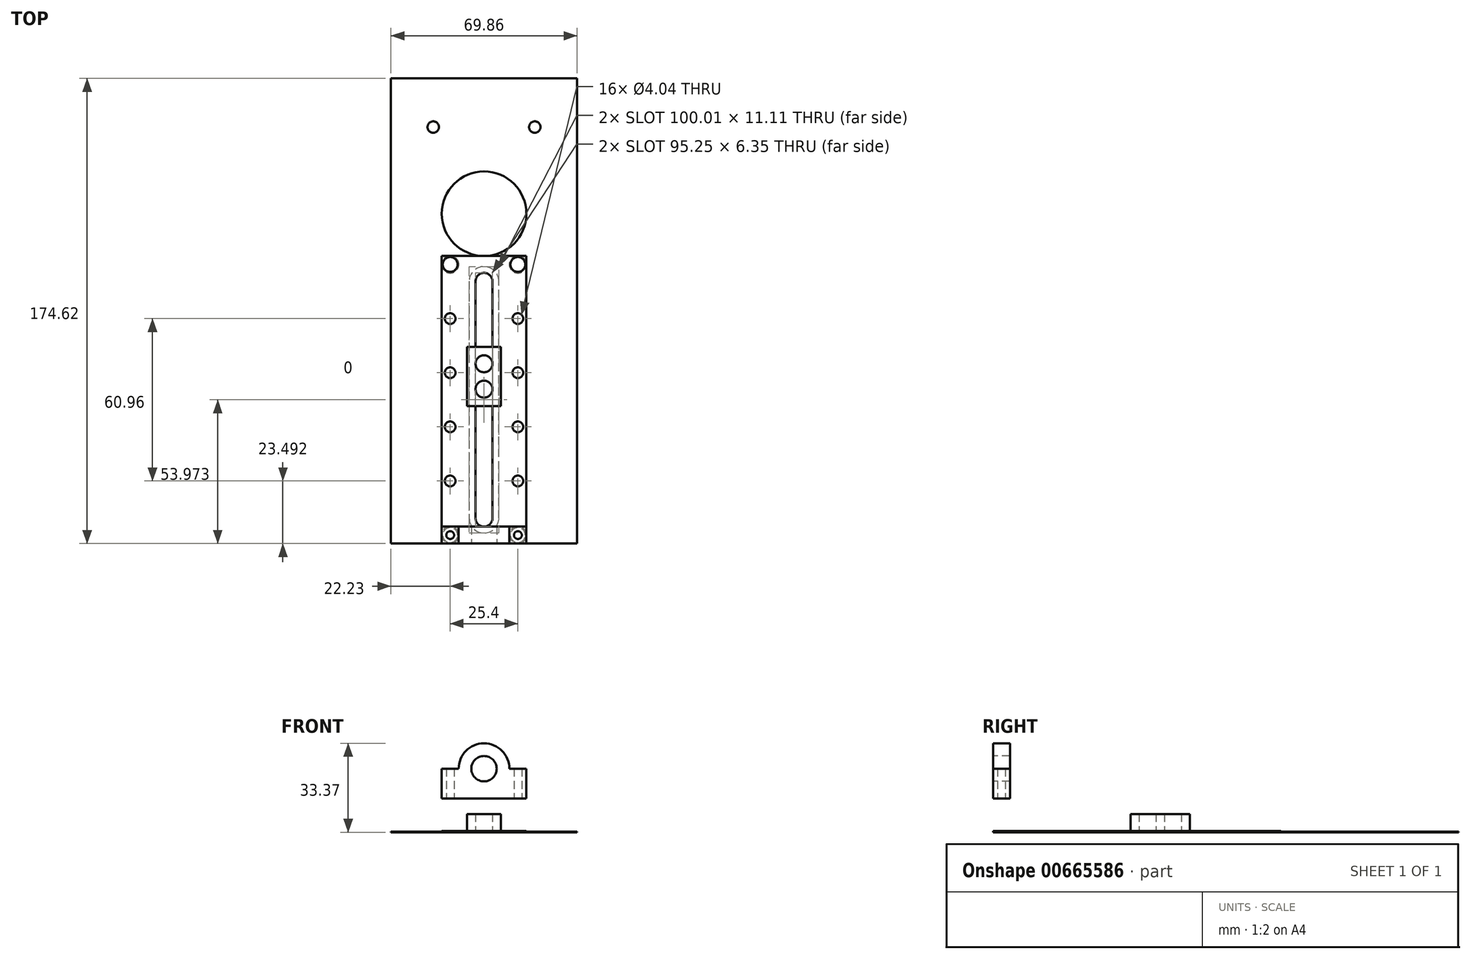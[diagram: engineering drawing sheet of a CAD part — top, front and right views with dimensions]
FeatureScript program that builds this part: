
annotation { "Feature Type Name" : "Feature", "Feature Type Description" : "" }
export const myFeature = defineFeature(function(context is Context, id is Id, definition is map)
    precondition{}
    {
        {
            assignVariable(context, id + "F0", {"name" : "baseThickness", "anyValue" : 0.25});
        }
        {
            assignVariable(context, id + "F1", {"name" : "topThickness", "anyValue" : 0.25});
        }
        {
            var Q0;
            Q0=qCreatedBy(makeId("Top.planeOp"),FACE);
            var sketch = newSketch(context, id + "F2", { "sketchPlane" : qUnion([Q0])});
            skLineSegment(sketch, "E0.bottom", {"start": v(-34.92, 87.31) * mm, "end": v(34.92, 87.31) * mm});
            skLineSegment(sketch, "E0.top", {"start": v(-34.92, -87.31) * mm, "end": v(34.92, -87.31) * mm});
            skLineSegment(sketch, "E0.left", {"start": v(-34.92, 87.31) * mm, "end": v(-34.92, -87.31) * mm});
            skLineSegment(sketch, "E0.right", {"start": v(34.93, 87.31) * mm, "end": v(34.93, -87.31) * mm});
            skCircle(sketch, "E1", {"center": v(0, 36.51) * mm, "radius": 15.88 * mm});
            skCircle(sketch, "E2", {"center": v(-19.05, 69.02) * mm, "radius": 2.15 * mm});
            skCircle(sketch, "E3", {"center": v(19.05, 69.02) * mm, "radius": 2.15 * mm});
            skArc(sketch, "E4", {"start": v(5.56, 11.11) * mm, "mid": v(0, 16.67) * mm, "end": v(-5.56, 11.11) * mm});
            skArc(sketch, "E5", {"start": v(-5.56, -77.79) * mm, "mid": v(0, -83.34) * mm, "end": v(5.56, -77.79) * mm});
            skLineSegment(sketch, "E6", {"start": v(-5.56, 11.11) * mm, "end": v(-5.56, -77.79) * mm});
            skLineSegment(sketch, "E7", {"start": v(5.56, -77.79) * mm, "end": v(5.56, 11.11) * mm});
            skCircle(sketch, "E8", {"center": v(-12.7, 17.46) * mm, "radius": 2.25 * mm, "construction": true});
            skCircle(sketch, "E9", {"center": v(12.7, 17.46) * mm, "radius": 2.25 * mm, "construction": true});
            skCircle(sketch, "E10", {"center": v(12.7, -84.14) * mm, "radius": 2.25 * mm, "construction": true});
            skCircle(sketch, "E11", {"center": v(-12.7, -84.14) * mm, "radius": 2.25 * mm, "construction": true});
            skSolve(sketch);
        }
        {
            var Q0;
            Q0=makeQuery(id+"F2.imprint","IMPRINT",FACE,{"disambiguationData":[TD([[makeQuery(id+"F2.imprint","IMPRINT",EDGE,{"derivedFrom":sQuery(id+"F2.wireOp",EDGE,"E0.bottom")}),-1.0]])]});
            extrude(context, id + "F3", {"entities" : qUnion([Q0]), "depth" : (getVariable(context, 'baseThickness')) * mm, "offsetDistance" : 25.4 * mm});
        }
        {
            var Q0;
            Q0=makeQuery(id+"F3.opExtrude","CAP_FACE",FACE,{"disambiguationData":[OSD([sQuery(id+"F2.wireOp",EDGE,"E0.bottom"),sQuery(id+"F2.wireOp",EDGE,"E0.top"),sQuery(id+"F2.wireOp",EDGE,"E0.left"),sQuery(id+"F2.wireOp",EDGE,"E0.right"),sQuery(id+"F2.wireOp",EDGE,"E1"),sQuery(id+"F2.wireOp",EDGE,"E2"),sQuery(id+"F2.wireOp",EDGE,"E3"),sQuery(id+"F2.wireOp",EDGE,"E4"),sQuery(id+"F2.wireOp",EDGE,"E5"),sQuery(id+"F2.wireOp",EDGE,"E6"),sQuery(id+"F2.wireOp",EDGE,"E7")])],"isStart":false});
            var sketch = newSketch(context, id + "F4", { "sketchPlane" : qUnion([Q0])});
            skArc(sketch, "E12", {"start": v(3.17, 11.11) * mm, "mid": v(0, 14.29) * mm, "end": v(-3.17, 11.11) * mm});
            skArc(sketch, "E13", {"start": v(-3.18, -77.79) * mm, "mid": v(0, -80.96) * mm, "end": v(3.18, -77.79) * mm});
            skLineSegment(sketch, "E14", {"start": v(-3.18, -77.79) * mm, "end": v(-3.17, 11.11) * mm});
            skLineSegment(sketch, "E15", {"start": v(3.17, 11.11) * mm, "end": v(3.18, -77.79) * mm});
            skLineSegment(sketch, "E16", {"start": v(-15.87, 20.64) * mm, "end": v(15.87, 20.64) * mm});
            skLineSegment(sketch, "E17", {"start": v(15.87, 20.64) * mm, "end": v(15.88, -87.31) * mm});
            skLineSegment(sketch, "E18", {"start": v(15.88, -87.31) * mm, "end": v(-15.88, -87.31) * mm});
            skLineSegment(sketch, "E19", {"start": v(-15.88, -87.31) * mm, "end": v(-15.88, 20.64) * mm});
            skCircle(sketch, "E20", {"center": v(-12.7, -2.86) * mm, "radius": 1.56 * mm, "construction": true});
            skCircle(sketch, "E21", {"center": v(-12.7, -43.5) * mm, "radius": 1.56 * mm, "construction": true});
            skCircle(sketch, "E22", {"center": v(-12.7, -63.82) * mm, "radius": 1.56 * mm, "construction": true});
            skCircle(sketch, "E23", {"center": v(-12.7, -23.18) * mm, "radius": 1.56 * mm, "construction": true});
            skCircle(sketch, "E24.MirrorC", {"center": v(12.7, -2.86) * mm, "radius": 1.56 * mm, "construction": true});
            skCircle(sketch, "E25.MirrorC", {"center": v(12.7, -23.18) * mm, "radius": 1.56 * mm, "construction": true});
            skCircle(sketch, "E26.MirrorC", {"center": v(12.7, -43.5) * mm, "radius": 1.56 * mm, "construction": true});
            skCircle(sketch, "E27.MirrorC", {"center": v(12.7, -63.82) * mm, "radius": 1.56 * mm, "construction": true});
            skLineSegment(sketch, "E28", {"start": v(-12.7, 17.46) * mm, "end": v(-12.7, -2.86) * mm, "construction": true});
            skLineSegment(sketch, "E29", {"start": v(-12.7, -23.18) * mm, "end": v(-12.7, -2.86) * mm, "construction": true});
            skLineSegment(sketch, "E30", {"start": v(-12.7, -23.18) * mm, "end": v(-12.7, -43.5) * mm, "construction": true});
            skLineSegment(sketch, "E31", {"start": v(-12.7, -43.5) * mm, "end": v(-12.7, -63.82) * mm, "construction": true});
            skLineSegment(sketch, "E32", {"start": v(-12.7, -63.82) * mm, "end": v(-12.7, -84.14) * mm, "construction": true});
            skSolve(sketch);
        }
        {
            var Q0;
            Q0 = qSketchRegion(id + "F4", true);
            extrude(context, id + "F5", {"entities" : qUnion([Q0]), "depth" : (getVariable(context, 'topThickness')) * mm, "offsetDistance" : 25.4 * mm});
        }
        {
            var Q0;
            Q0=sQuery(id+"F4.wireOp",VERTEX,"E31.end");
            var Q1;
            Q1=sQuery(id+"F4.wireOp",VERTEX,"E21.center");
            var Q2;
            Q2=sQuery(id+"F4.wireOp",VERTEX,"E30.start");
            var Q3;
            Q3=sQuery(id+"F4.wireOp",VERTEX,"E29.end");
            var Q4;
            Q4=sQuery(id+"F4.wireOp",VERTEX,"E24.MirrorC.center");
            var Q5;
            Q5=sQuery(id+"F4.wireOp",VERTEX,"E25.MirrorC.center");
            var Q6;
            Q6=sQuery(id+"F4.wireOp",VERTEX,"E26.MirrorC.center");
            var Q7;
            Q7=sQuery(id+"F4.wireOp",VERTEX,"E27.MirrorC.center");
            var Q8;
            Q8=makeQuery(id+"F5.opExtrude","SWEPT_BODY",BODY,{"disambiguationData":[OSD([sQuery(id+"F4.wireOp",EDGE,"E12"),sQuery(id+"F4.wireOp",EDGE,"E13"),sQuery(id+"F4.wireOp",EDGE,"E14"),sQuery(id+"F4.wireOp",EDGE,"E15"),sQuery(id+"F4.wireOp",EDGE,"E16"),sQuery(id+"F4.wireOp",EDGE,"E17"),sQuery(id+"F4.wireOp",EDGE,"E18"),sQuery(id+"F4.wireOp",EDGE,"E19")])]});
            hole(context, id + "F6", {"style" : HoleStyle.SIMPLE, "endStyle" : HoleEndStyle.THROUGH, "oppositeDirection" : true, "standardTappedOrClearance" : lookupTablePath({ "standard" : "ANSI", "engagement" : "75%", "pitch" : "32 tpi", "size" : "#10", "type" : "Tapped" }), "standardBlindInLast" : lookupTablePath({ "standard" : "ANSI", "engagement" : "75%", "pitch" : "32 tpi", "size" : "#10", "type" : "Tapped" }), "holeDiameter" : 4.04 * mm, "majorDiameter" : 4.83 * mm, "showTappedDepth" : true, "isTappedThrough" : true, "tappedDepth" : 12.7 * mm, "tapClearance" : 3, "locations" : qUnion([Q0, Q1, Q2, Q3, Q4, Q5, Q6, Q7]), "scope" : qUnion([Q8])});
        }
        {
            var Q0;
            Q0=makeQuery(id+"F5.opExtrude","SWEPT_FACE",FACE,{"disambiguationData":[OSD([sQuery(id+"F4.wireOp",EDGE,"E18")])]});
            var sketch = newSketch(context, id + "F7", { "sketchPlane" : qUnion([Q0])});
            skCircle(sketch, "E33", {"center": v(0, 23.84) * mm, "radius": 4.76 * mm});
            skLineSegment(sketch, "E34", {"start": v(-15.88, 12.7) * mm, "end": v(-15.88, 23.84) * mm});
            skLineSegment(sketch, "E35", {"start": v(15.88, 12.7) * mm, "end": v(15.88, 23.84) * mm});
            skArc(sketch, "E36", {"start": v(9.53, 23.84) * mm, "mid": v(0, 33.37) * mm, "end": v(-9.53, 23.84) * mm});
            skLineSegment(sketch, "E37", {"start": v(-9.53, 23.84) * mm, "end": v(-15.88, 23.84) * mm});
            skLineSegment(sketch, "E38", {"start": v(9.53, 23.84) * mm, "end": v(15.88, 23.84) * mm});
            skLineSegment(sketch, "E39", {"start": v(-15.88, 12.7) * mm, "end": v(15.88, 12.7) * mm});
            skSolve(sketch);
        }
        {
            var Q0;
            Q0 = qSketchRegion(id + "F7", true);
            extrude(context, id + "F8", {"entities" : qUnion([Q0]), "oppositeDirection" : true, "depth" : 6.35 * mm, "offsetDistance" : 25.4 * mm});
        }
        {
            var Q0;
            Q0=sQuery(id+"F2.wireOp",VERTEX,"E10.center");
            var Q1;
            Q1=sQuery(id+"F2.wireOp",VERTEX,"E11.center");
            var Q2;
            Q2=sQuery(id+"F2.wireOp",VERTEX,"E8.center");
            var Q3;
            Q3=sQuery(id+"F2.wireOp",VERTEX,"E9.center");
            var Q4;
            Q4=makeQuery(id+"F3.opExtrude","SWEPT_BODY",BODY,{"disambiguationData":[OSD([sQuery(id+"F2.wireOp",EDGE,"E0.bottom"),sQuery(id+"F2.wireOp",EDGE,"E0.top"),sQuery(id+"F2.wireOp",EDGE,"E0.left"),sQuery(id+"F2.wireOp",EDGE,"E0.right"),sQuery(id+"F2.wireOp",EDGE,"E1"),sQuery(id+"F2.wireOp",EDGE,"E2"),sQuery(id+"F2.wireOp",EDGE,"E3"),sQuery(id+"F2.wireOp",EDGE,"E4"),sQuery(id+"F2.wireOp",EDGE,"E5"),sQuery(id+"F2.wireOp",EDGE,"E6"),sQuery(id+"F2.wireOp",EDGE,"E7")])]});
            var Q5;
            Q5=makeQuery(id+"F5.opExtrude","SWEPT_BODY",BODY,{"disambiguationData":[OSD([sQuery(id+"F4.wireOp",EDGE,"E12"),sQuery(id+"F4.wireOp",EDGE,"E13"),sQuery(id+"F4.wireOp",EDGE,"E14"),sQuery(id+"F4.wireOp",EDGE,"E15"),sQuery(id+"F4.wireOp",EDGE,"E16"),sQuery(id+"F4.wireOp",EDGE,"E17"),sQuery(id+"F4.wireOp",EDGE,"E18"),sQuery(id+"F4.wireOp",EDGE,"E19")])]});
            var Q6;
            Q6=makeQuery(id+"F8.opExtrude","SWEPT_BODY",BODY,{"disambiguationData":[OSD([sQuery(id+"F7.wireOp",EDGE,"E33"),sQuery(id+"F7.wireOp",EDGE,"E34"),sQuery(id+"F7.wireOp",EDGE,"E35"),sQuery(id+"F7.wireOp",EDGE,"E36"),sQuery(id+"F7.wireOp",EDGE,"E37"),sQuery(id+"F7.wireOp",EDGE,"E38"),sQuery(id+"F7.wireOp",EDGE,"E39")])]});
            hole(context, id + "F9", {"style" : HoleStyle.C_SINK, "endStyle" : HoleEndStyle.THROUGH, "oppositeDirection" : true, "standardTappedOrClearance" : lookupTablePath({ "standard" : "ANSI", "fit" : "Close", "size" : "#4", "type" : "Clearance" }), "standardBlindInLast" : lookupTablePath({ "fit" : "Close", "standard" : "ANSI", "size" : "#4", "type" : "Clearance" }), "holeDiameter" : 2.95 * mm, "cSinkDiameter" : 6.48 * mm, "cSinkAngle" : 82 * degree, "majorDiameter" : 6.35 * mm, "isTappedThrough" : true, "tappedDepth" : 12.7 * mm, "tapClearance" : 3, "locations" : qUnion([Q0, Q1, Q2, Q3]), "scope" : qUnion([Q4, Q5, Q6])});
        }
        {
            var Q0;
            Q0=makeQuery(id+"F5.opExtrude","CAP_FACE",FACE,{"disambiguationData":[OSD([sQuery(id+"F4.wireOp",EDGE,"E12"),sQuery(id+"F4.wireOp",EDGE,"E13"),sQuery(id+"F4.wireOp",EDGE,"E14"),sQuery(id+"F4.wireOp",EDGE,"E15"),sQuery(id+"F4.wireOp",EDGE,"E16"),sQuery(id+"F4.wireOp",EDGE,"E17"),sQuery(id+"F4.wireOp",EDGE,"E18"),sQuery(id+"F4.wireOp",EDGE,"E19")])],"isStart":false});
            var sketch = newSketch(context, id + "F10", { "sketchPlane" : qUnion([Q0])});
            skLineSegment(sketch, "E40.bottom", {"start": v(-6.35, -13.47) * mm, "end": v(6.35, -13.47) * mm});
            skLineSegment(sketch, "E40.top", {"start": v(-6.35, -35.7) * mm, "end": v(6.35, -35.7) * mm});
            skLineSegment(sketch, "E40.left", {"start": v(-6.35, -13.47) * mm, "end": v(-6.35, -35.7) * mm});
            skLineSegment(sketch, "E40.right", {"start": v(6.35, -13.47) * mm, "end": v(6.35, -35.7) * mm});
            skCircle(sketch, "E41", {"center": v(0, -19.82) * mm, "radius": 3.18 * mm});
            skCircle(sketch, "E42", {"center": v(0, -29.34) * mm, "radius": 3.18 * mm});
            skSolve(sketch);
        }
        {
            var Q0;
            Q0 = qSketchRegion(id + "F10", true);
            extrude(context, id + "F11", {"entities" : qUnion([Q0]), "depth" : 6.35 * mm, "offsetDistance" : 25.4 * mm});
        }
    });
